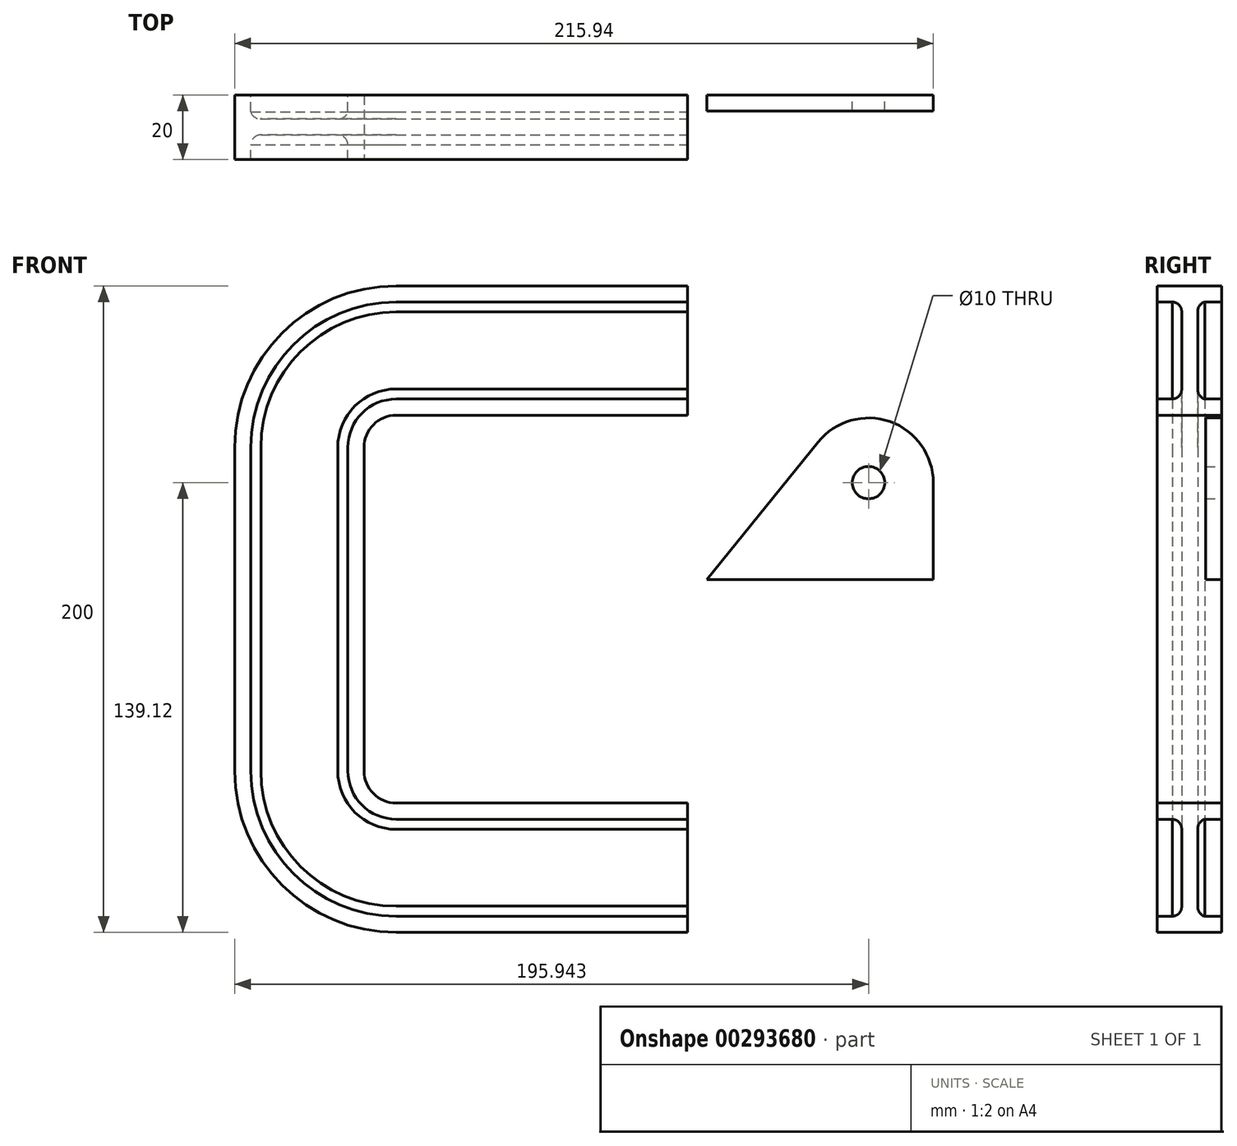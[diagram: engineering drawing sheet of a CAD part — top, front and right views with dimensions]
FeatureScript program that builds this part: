
annotation { "Feature Type Name" : "Feature", "Feature Type Description" : "" }
export const myFeature = defineFeature(function(context is Context, id is Id, definition is map)
    precondition{}
    {
        {
            var Q0;
            Q0=qCreatedBy(makeId("Front.planeOp"),FACE);
            var sketch = newSketch(context, id + "F0", { "sketchPlane" : qUnion([Q0])});
            skLineSegment(sketch, "E0", {"start": v(-100, 0) * mm, "end": v(-100, 50) * mm});
            skLineSegment(sketch, "E1", {"start": v(-90, 60) * mm, "end": v(0, 60) * mm});
            skPoint(sketch, "E2.visualSharp", {"position": v(-100, 60) * mm});
            skArc(sketch, "E2.filletArc", {"start": v(-90, 60) * mm, "mid": v(-97.07, 57.07) * mm, "end": v(-100, 50) * mm});
            skArc(sketch, "E3.MirrorCS", {"start": v(-90, -60) * mm, "mid": v(-97.07, -57.07) * mm, "end": v(-100, -50) * mm});
            skLineSegment(sketch, "E4.MirrorCS", {"start": v(-90, -60) * mm, "end": v(0, -60) * mm});
            skLineSegment(sketch, "E5.MirrorCS", {"start": v(-100, 0) * mm, "end": v(-100, -50) * mm});
            skPoint(sketch, "E6.MirrorP", {"position": v(-100, -60) * mm});
            skSolve(sketch);
        }
        {
            var Q0;
            Q0=qCreatedBy(makeId("Right.planeOp"),FACE);
            var sketch = newSketch(context, id + "F1", { "sketchPlane" : qUnion([Q0])});
            skLineSegment(sketch, "E7", {"start": v(0, 60) * mm, "end": v(-20, 60) * mm});
            skLineSegment(sketch, "E8", {"start": v(-20, 60) * mm, "end": v(-20, 65) * mm});
            skLineSegment(sketch, "E9", {"start": v(-20, 65) * mm, "end": v(-15.3, 65) * mm});
            skLineSegment(sketch, "E10", {"start": v(0, 65) * mm, "end": v(0, 60) * mm});
            skLineSegment(sketch, "E11.trimOffspring", {"start": v(-5.2, 65) * mm, "end": v(0, 65) * mm});
            skPoint(sketch, "E12.start.orphan", {"position": v(-10, 60) * mm});
            skArc(sketch, "E13", {"start": v(-15.3, 65) * mm, "mid": v(-13.18, 65.94) * mm, "end": v(-12.36, 68.11) * mm});
            skArc(sketch, "E14", {"start": v(-7.36, 68.08) * mm, "mid": v(-6.83, 66.16) * mm, "end": v(-5.2, 65) * mm});
            skPoint(sketch, "E15.orphan", {"position": v(-12.36, 65) * mm});
            skPoint(sketch, "E16.orphan", {"position": v(-7.36, 65) * mm});
            skPoint(sketch, "E17.MirrorP", {"position": v(-12.36, 92.37) * mm});
            skArc(sketch, "E18.MirrorCS", {"start": v(-7.36, 91.92) * mm, "mid": v(-6.83, 93.84) * mm, "end": v(-5.2, 95) * mm});
            skPoint(sketch, "E19.MirrorP", {"position": v(-10, 97.37) * mm});
            skLineSegment(sketch, "E20.MirrorCS", {"start": v(0, 100) * mm, "end": v(-20, 100) * mm});
            skLineSegment(sketch, "E21.MirrorCS", {"start": v(-20, 100) * mm, "end": v(-20, 95) * mm});
            skLineSegment(sketch, "E22.MirrorCS", {"start": v(0, 95) * mm, "end": v(0, 100) * mm});
            skLineSegment(sketch, "E23.MirrorCS", {"start": v(-20, 95) * mm, "end": v(-15.3, 95) * mm});
            skLineSegment(sketch, "E24.MirrorCS", {"start": v(-5.2, 95) * mm, "end": v(0, 95) * mm});
            skArc(sketch, "E25.MirrorCS", {"start": v(-15.3, 95) * mm, "mid": v(-13.18, 94.06) * mm, "end": v(-12.36, 91.89) * mm});
            skPoint(sketch, "E26.MirrorP", {"position": v(-7.36, 92.37) * mm});
            skLineSegment(sketch, "E27", {"start": v(-12.36, 91.89) * mm, "end": v(-12.36, 68.11) * mm});
            skLineSegment(sketch, "E28", {"start": v(-7.36, 91.92) * mm, "end": v(-7.36, 68.08) * mm});
            skSolve(sketch);
        }
        {
            var Q0;
            Q0=makeQuery(id+"F1.imprint","IMPRINT",FACE,{"disambiguationData":[TD([[makeQuery(id+"F1.imprint","IMPRINT",EDGE,{"derivedFrom":sQuery(id+"F1.wireOp",EDGE,"E7")}),-1.0]])]});
            var Q1;
            Q1=sQuery(id+"F0.wireOp",EDGE,"E1");
            var Q2;
            Q2=sQuery(id+"F0.wireOp",EDGE,"E0");
            var Q3;
            Q3=sQuery(id+"F0.wireOp",EDGE,"E2.filletArc");
            var Q4;
            Q4=sQuery(id+"F0.wireOp",EDGE,"E5.MirrorCS");
            var Q5;
            Q5=sQuery(id+"F0.wireOp",EDGE,"E3.MirrorCS");
            var Q6;
            Q6=sQuery(id+"F0.wireOp",EDGE,"E4.MirrorCS");
            sweep(context, id + "F2", {"profiles" : qUnion([Q0]), "path" : qUnion([Q1, Q2, Q3, Q4, Q5, Q6])});
        }
        {
            var Q0;
            Q0=qCreatedBy(makeId("Front.planeOp"),FACE);
            var sketch = newSketch(context, id + "F3", { "sketchPlane" : qUnion([Q0])});
            skLineSegment(sketch, "E29", {"start": v(5.94, 9.12) * mm, "end": v(75.94, 9.12) * mm});
            skLineSegment(sketch, "E30", {"start": v(75.94, 9.12) * mm, "end": v(75.94, 39.12) * mm});
            skArc(sketch, "E31", {"start": v(75.94, 39.12) * mm, "mid": v(62.62, 57.97) * mm, "end": v(40.4, 51.7) * mm});
            skLineSegment(sketch, "E32", {"start": v(5.94, 9.12) * mm, "end": v(40.4, 51.7) * mm});
            skCircle(sketch, "E33", {"center": v(55.94, 39.12) * mm, "radius": 5 * mm});
            skSolve(sketch);
        }
        {
            var Q0;
            Q0=makeQuery(id+"F3.imprint","IMPRINT",FACE,{"disambiguationData":[TD([[makeQuery(id+"F3.imprint","IMPRINT",EDGE,{"derivedFrom":sQuery(id+"F3.wireOp",EDGE,"E29")}),1.0]])]});
            extrude(context, id + "F4", {"entities" : qUnion([Q0]), "depth" : 5 * mm});
        }
    });
